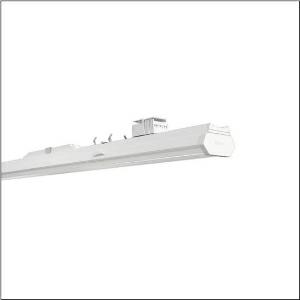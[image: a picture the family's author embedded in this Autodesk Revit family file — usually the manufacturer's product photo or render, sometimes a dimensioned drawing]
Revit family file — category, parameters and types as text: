
# Revit family: licross_r__11_protected_mo_51tp127n485g_ff31
name_source: partatom
category: Lighting Fixtures
units: mm (PartAtom-declared; Revit-internal decimal feet)

## family parameters
Cut with Voids When Loaded = No
Host = Face
Light Source = No
Part Type = Normal
Room Calculation Point = No
Round Connector Dimension = Use Diameter
Shared = No

## types (1)
- Licross® 11 Protected MO (1 x LED, 8720 lm, 48.6 W, 4000K)
    Apparent Load = 49 VA
    CIE Flux Codes = 73 92 98 99 100
    Color Rendering = 80
    Color Temperature = 4000K
    Default Elevation = 1800 mm
    Description = Licross® 11 Protected MO, luminaire insert, of sheet steel, galvanised, coil coated, white, length: 1.500mm, width: 90mm, height: 101mm, LED rated luminous flux: 8.720lm, light colour: 840, control gear: ON/OFF, with plug, 3-pole, with phase selection, mains connection: 220..240V, AC, 50/60Hz, rated input power: 49W, internal wiring halogen-free, primary light control with lens, of plastic, primary optical cover: cover, of PMMA, light emission: direct distribution, primary light characteristic: symmetric, protection rating (complete): IP64, insulation class (complete): insulation class I (protective earthing), certification: CE, ENEC, VDE, UKCA, protection symbol: D if used in an environment with conductive dust loads with corresponding accessories, impact resistance: IK06, permissible ambient temperature for indoor applications: -25..+35°C, corresponds to IFS (International Featured Standards) requirements for safety and quality in the food industry, reducing of maximum allowable ambient temperature of 5°C with ceiling mounting, LABS conformity tested according to VDMA 24364:2018-05, packaging unit: 1 piece
    Height = 92 mm
    Lamp = 1 x LED
    Lamp Light Flux = 8720 lm
    Lamp Power = 48.6 W
    Lamp count = 1
    Length = 1500 mm
    Luminous efficacy = 179 lm/W
    Manufacturer = Siteco
    ModVariant = No
    Model = 51TP127N485G
    Mounting Place = Ceiling
    Mounting Type = Pendant
    Number of Poles = 1
    OnlyDefault = Yes
    Power Factor = 1
    Product Name = Licross® 11 Protected MO
    Product group = luminaire insert | ceiling pendant
    ProductGroupID = 902
    Protection Class = Protection class I
    Protection Degree = IP 64
    RLX_Detail_Level = 1
    RLX_Emergency_Light_Flux = 0 lm
    RLX_Emergency_Type = 0
    RLX_Emergency_Type_DB = No
    RlxData = <blob elided: 20689 chars, md5=a9abf3f9>
    Socket = socket
    Standby Power = 0 W
    System Light Flux = 8720 lm
    System Power = 49 W
    Type Comments = Product without accessories
    Type Image = l_1256148.jpg
    URL = http://relux.com
    VarID = ---
    Voltage = 0 V
    Weight = 0.00 kg
    Width = 88 mm

## geometry (parser evidence)
native form markers: Blend x4, Sweep x10
no freeform markers — native parametric forms only
